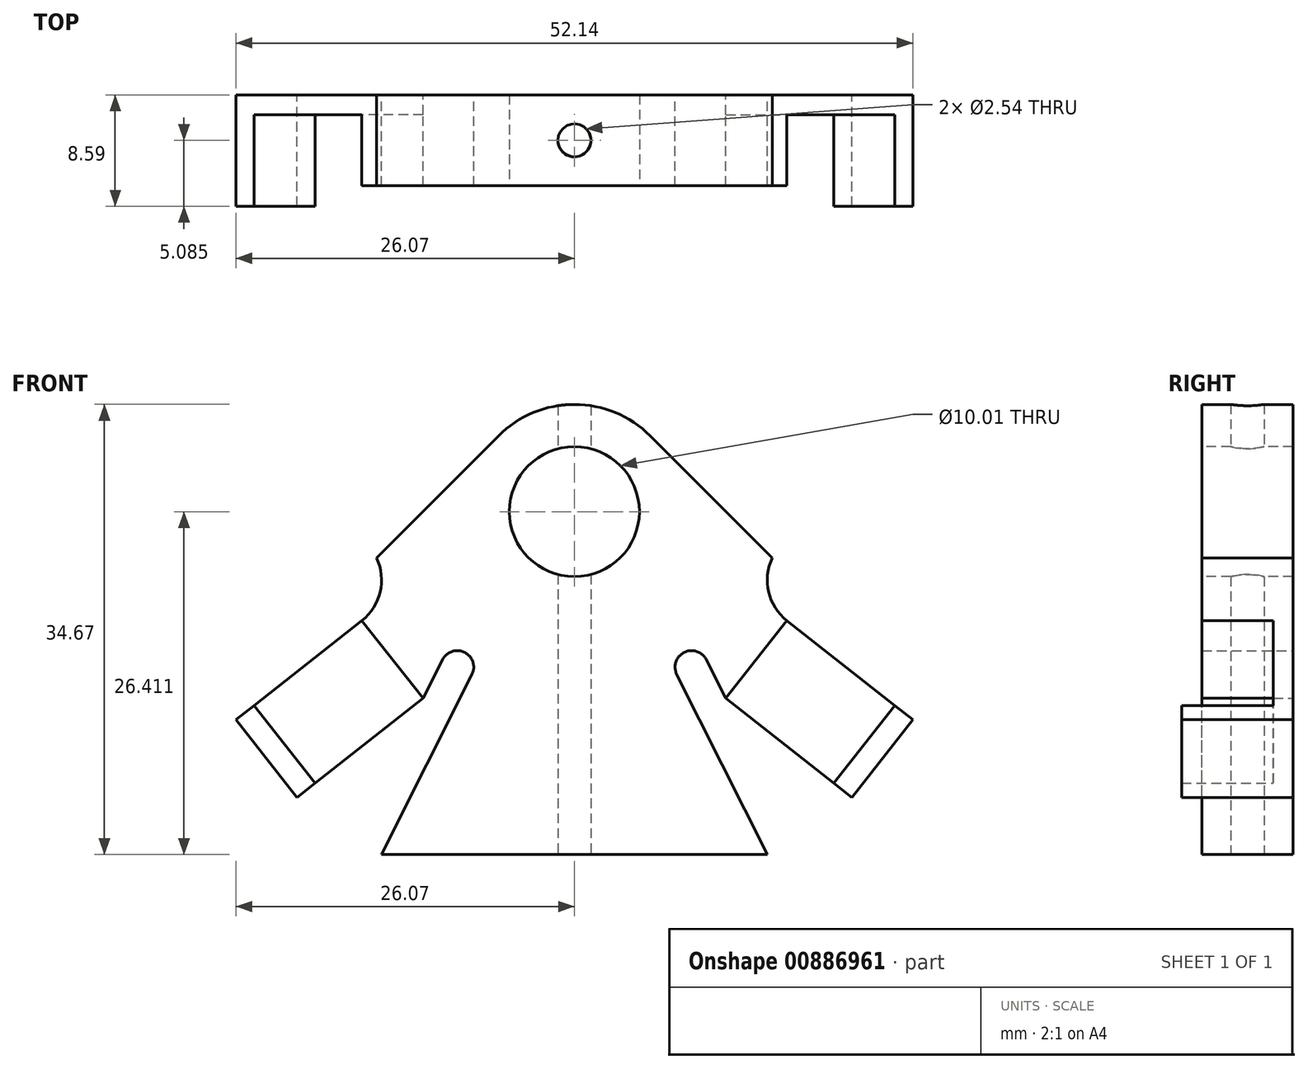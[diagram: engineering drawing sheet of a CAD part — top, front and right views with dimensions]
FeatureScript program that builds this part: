
annotation { "Feature Type Name" : "Feature", "Feature Type Description" : "" }
export const myFeature = defineFeature(function(context is Context, id is Id, definition is map)
    precondition{}
    {
        {
            var Q0;
            Q0=qCreatedBy(makeId("Front.planeOp"),FACE);
            var sketch = newSketch(context, id + "F0", { "sketchPlane" : qUnion([Q0])});
            skLineSegment(sketch, "E0", {"start": v(0, 0) * mm, "end": v(14.86, 0) * mm});
            skLineSegment(sketch, "E1", {"start": v(14.86, 0) * mm, "end": v(7.9, 13.87) * mm});
            skArc(sketch, "E2", {"start": v(7.9, 13.87) * mm, "mid": v(8.46, 15.57) * mm, "end": v(10.16, 15) * mm});
            skLineSegment(sketch, "E3", {"start": v(10.16, 15) * mm, "end": v(11.65, 12.03) * mm});
            skLineSegment(sketch, "E4", {"start": v(11.65, 12.03) * mm, "end": v(19.96, 5.5) * mm});
            skLineSegment(sketch, "E5", {"start": v(19.96, 5.5) * mm, "end": v(21.36, 4.4) * mm});
            skLineSegment(sketch, "E6", {"start": v(21.36, 4.4) * mm, "end": v(26.07, 10.39) * mm});
            skLineSegment(sketch, "E7", {"start": v(26.07, 10.39) * mm, "end": v(16.37, 18.02) * mm});
            skArc(sketch, "E8", {"start": v(16.37, 18.02) * mm, "mid": v(14.96, 20.24) * mm, "end": v(15.24, 22.85) * mm});
            skLineSegment(sketch, "E9", {"start": v(15.24, 22.85) * mm, "end": v(0, 38.09) * mm});
            skLineSegment(sketch, "E10", {"start": v(0, 38.09) * mm, "end": v(0, 0) * mm});
            skLineSegment(sketch, "E11.MirrorCS", {"start": v(-19.96, 5.5) * mm, "end": v(-21.36, 4.4) * mm});
            skLineSegment(sketch, "E12.MirrorCS", {"start": v(0, 0) * mm, "end": v(-14.86, 0) * mm});
            skLineSegment(sketch, "E13.MirrorCS", {"start": v(-14.86, 0) * mm, "end": v(-7.9, 13.87) * mm});
            skArc(sketch, "E14.MirrorCS", {"start": v(-7.9, 13.87) * mm, "mid": v(-8.46, 15.57) * mm, "end": v(-10.16, 15) * mm});
            skLineSegment(sketch, "E15.MirrorCS", {"start": v(-10.16, 15) * mm, "end": v(-11.65, 12.03) * mm});
            skLineSegment(sketch, "E16.MirrorCS", {"start": v(-11.65, 12.03) * mm, "end": v(-19.96, 5.5) * mm});
            skLineSegment(sketch, "E17.MirrorCS", {"start": v(-21.36, 4.4) * mm, "end": v(-26.07, 10.39) * mm});
            skLineSegment(sketch, "E18.MirrorCS", {"start": v(-26.07, 10.39) * mm, "end": v(-16.37, 18.02) * mm});
            skArc(sketch, "E19.MirrorCS", {"start": v(-16.37, 18.02) * mm, "mid": v(-14.96, 20.24) * mm, "end": v(-15.24, 22.85) * mm});
            skLineSegment(sketch, "E20.MirrorCS", {"start": v(-15.24, 22.85) * mm, "end": v(0, 38.09) * mm});
            skSolve(sketch);
        }
        {
            var Q0;
            Q0=makeQuery(id+"F0.imprint","IMPRINT",FACE,{"disambiguationData":[TD([[makeQuery(id+"F0.imprint","IMPRINT",EDGE,{"derivedFrom":sQuery(id+"F0.wireOp",EDGE,"E0")}),1.0]])]});
            var Q1;
            Q1=makeQuery(id+"F0.imprint","IMPRINT",FACE,{"disambiguationData":[TD([[makeQuery(id+"F0.imprint","IMPRINT",EDGE,{"derivedFrom":sQuery(id+"F0.wireOp",EDGE,"E10")}),-1.0]])]});
            extrude(context, id + "F1", {"entities" : qUnion([Q0, Q1]), "depth" : 1.52 * mm, "offsetDistance" : 25.4 * mm});
        }
        {
            var Q0;
            Q0=makeQuery(id+"F1.opExtrude","SWEPT_EDGE",EDGE,{"disambiguationData":[OSD([sQuery(id+"F0.wireOp",EDGE,"E9"),sQuery(id+"F0.wireOp",EDGE,"E10"),sQuery(id+"F0.wireOp",EDGE,"E20.MirrorCS")])]});
            fillet(context, id + "F2", {"entities" : qUnion([Q0]), "radius" : 8.25 * mm, "tangentPropagation" : true, "allowEdgeOverflow" : false});
        }
        {
            var Q0;
            Q0=makeQuery(id+"F1.opExtrude","CAP_FACE",FACE,{"disambiguationData":[OSD([sQuery(id+"F0.wireOp",EDGE,"E0"),sQuery(id+"F0.wireOp",EDGE,"E1"),sQuery(id+"F0.wireOp",EDGE,"E2"),sQuery(id+"F0.wireOp",EDGE,"E3"),sQuery(id+"F0.wireOp",EDGE,"E4"),sQuery(id+"F0.wireOp",EDGE,"E5"),sQuery(id+"F0.wireOp",EDGE,"E6"),sQuery(id+"F0.wireOp",EDGE,"E7"),sQuery(id+"F0.wireOp",EDGE,"E8"),sQuery(id+"F0.wireOp",EDGE,"E9"),sQuery(id+"F0.wireOp",EDGE,"E11.MirrorCS"),sQuery(id+"F0.wireOp",EDGE,"E12.MirrorCS"),sQuery(id+"F0.wireOp",EDGE,"E13.MirrorCS"),sQuery(id+"F0.wireOp",EDGE,"E14.MirrorCS"),sQuery(id+"F0.wireOp",EDGE,"E15.MirrorCS"),sQuery(id+"F0.wireOp",EDGE,"E16.MirrorCS"),sQuery(id+"F0.wireOp",EDGE,"E17.MirrorCS"),sQuery(id+"F0.wireOp",EDGE,"E18.MirrorCS"),sQuery(id+"F0.wireOp",EDGE,"E19.MirrorCS"),sQuery(id+"F0.wireOp",EDGE,"E20.MirrorCS")])],"isStart":false});
            var sketch = newSketch(context, id + "F3", { "sketchPlane" : qUnion([Q0])});
            skLineSegment(sketch, "E21", {"start": v(0, 34.67) * mm, "end": v(0, 26.41) * mm});
            skCircle(sketch, "E22", {"center": v(0, 26.41) * mm, "radius": 5 * mm});
            skSolve(sketch);
        }
        {
            var Q0;
            Q0=makeQuery(id+"F3.imprint","IMPRINT",FACE,{"disambiguationData":[TD([[makeQuery(id+"F3.imprint","IMPRINT",EDGE,{"derivedFrom":sQuery(id+"F3.wireOp",EDGE,"E22")}),1.0]])]});
            extrude(context, id + "F4", {"entities" : qUnion([Q0]), "operationType" : NewBodyOperationType.REMOVE, "oppositeDirection" : true, "depth" : 25.4 * mm, "offsetDistance" : 25.4 * mm});
        }
        {
            var Q0;
            Q0=makeQuery(id+"F1.opExtrude","CAP_FACE",FACE,{"disambiguationData":[OSD([sQuery(id+"F0.wireOp",EDGE,"E0"),sQuery(id+"F0.wireOp",EDGE,"E1"),sQuery(id+"F0.wireOp",EDGE,"E2"),sQuery(id+"F0.wireOp",EDGE,"E3"),sQuery(id+"F0.wireOp",EDGE,"E4"),sQuery(id+"F0.wireOp",EDGE,"E5"),sQuery(id+"F0.wireOp",EDGE,"E6"),sQuery(id+"F0.wireOp",EDGE,"E7"),sQuery(id+"F0.wireOp",EDGE,"E8"),sQuery(id+"F0.wireOp",EDGE,"E9"),sQuery(id+"F0.wireOp",EDGE,"E11.MirrorCS"),sQuery(id+"F0.wireOp",EDGE,"E12.MirrorCS"),sQuery(id+"F0.wireOp",EDGE,"E13.MirrorCS"),sQuery(id+"F0.wireOp",EDGE,"E14.MirrorCS"),sQuery(id+"F0.wireOp",EDGE,"E15.MirrorCS"),sQuery(id+"F0.wireOp",EDGE,"E16.MirrorCS"),sQuery(id+"F0.wireOp",EDGE,"E17.MirrorCS"),sQuery(id+"F0.wireOp",EDGE,"E18.MirrorCS"),sQuery(id+"F0.wireOp",EDGE,"E19.MirrorCS"),sQuery(id+"F0.wireOp",EDGE,"E20.MirrorCS")])],"isStart":false});
            var sketch = newSketch(context, id + "F5", { "sketchPlane" : qUnion([Q0])});
            skLineSegment(sketch, "E23.0.0", {"start": v(15.24, 22.85) * mm, "end": v(5.84, 32.25) * mm});
            skArc(sketch, "E23.0.1", {"start": v(5.84, 32.25) * mm, "mid": v(0, 34.67) * mm, "end": v(-5.84, 32.25) * mm});
            skLineSegment(sketch, "E23.0.2", {"start": v(-5.84, 32.25) * mm, "end": v(-15.24, 22.85) * mm});
            skArc(sketch, "E23.0.3", {"start": v(-15.24, 22.85) * mm, "mid": v(-14.96, 20.24) * mm, "end": v(-16.37, 18.02) * mm});
            skLineSegment(sketch, "E23.0.7", {"start": v(-11.65, 12.03) * mm, "end": v(-10.16, 15) * mm});
            skArc(sketch, "E23.0.8", {"start": v(-10.16, 15) * mm, "mid": v(-8.46, 15.57) * mm, "end": v(-7.9, 13.87) * mm});
            skLineSegment(sketch, "E23.0.9", {"start": v(-7.9, 13.87) * mm, "end": v(-14.86, 0) * mm});
            skLineSegment(sketch, "E23.0.10", {"start": v(-14.86, 0) * mm, "end": v(14.86, 0) * mm});
            skLineSegment(sketch, "E23.0.11", {"start": v(14.86, 0) * mm, "end": v(7.9, 13.87) * mm});
            skArc(sketch, "E23.0.12", {"start": v(7.9, 13.87) * mm, "mid": v(8.46, 15.57) * mm, "end": v(10.16, 15) * mm});
            skLineSegment(sketch, "E23.0.13", {"start": v(10.16, 15) * mm, "end": v(11.65, 12.03) * mm});
            skArc(sketch, "E23.0.17", {"start": v(16.37, 18.02) * mm, "mid": v(14.96, 20.24) * mm, "end": v(15.24, 22.85) * mm});
            skLineSegment(sketch, "E24", {"start": v(11.65, 12.03) * mm, "end": v(16.37, 18.02) * mm});
            skLineSegment(sketch, "E25", {"start": v(-11.65, 12.03) * mm, "end": v(-16.37, 18.02) * mm});
            skSolve(sketch);
        }
        {
            var Q0;
            Q0=makeQuery(id+"F5.imprint","IMPRINT",FACE,{"disambiguationData":[TD([[makeQuery(id+"F5.imprint","IMPRINT",EDGE,{"derivedFrom":sQuery(id+"F5.wireOp",EDGE,"E23.0.0")}),1.0]])]});
            extrude(context, id + "F6", {"entities" : qUnion([Q0]), "operationType" : NewBodyOperationType.ADD, "depth" : 5.5 * mm, "offsetDistance" : 25.4 * mm});
        }
        {
            var Q0;
            {var subQ0=sQuery(id+"F0.wireOp",EDGE,"E7");var subQ1=sQuery(id+"F0.wireOp",EDGE,"E6");var subQ2=sQuery(id+"F0.wireOp",EDGE,"E5");var subQ3=sQuery(id+"F0.wireOp",EDGE,"E4");var subQ4=sQuery(id+"F0.wireOp",EDGE,"E3");var subQ5=sQuery(id+"F0.wireOp",EDGE,"E8");Q0=makeQuery(id+"F6.boolean.opBoolean","SPLIT",FACE,{"disambiguationData":[TD([makeQuery(id+"F1.opExtrude","SWEPT_FACE",FACE,{"disambiguationData":[OSD([subQ4])]})])],"derivedFrom":makeQuery(id+"F1.opExtrude","CAP_FACE",FACE,{"disambiguationData":[OSD([sQuery(id+"F0.wireOp",EDGE,"E0"),sQuery(id+"F0.wireOp",EDGE,"E1"),sQuery(id+"F0.wireOp",EDGE,"E2"),subQ4,subQ3,subQ2,subQ1,subQ0,subQ5,sQuery(id+"F0.wireOp",EDGE,"E9"),sQuery(id+"F0.wireOp",EDGE,"E11.MirrorCS"),sQuery(id+"F0.wireOp",EDGE,"E12.MirrorCS"),sQuery(id+"F0.wireOp",EDGE,"E13.MirrorCS"),sQuery(id+"F0.wireOp",EDGE,"E14.MirrorCS"),sQuery(id+"F0.wireOp",EDGE,"E15.MirrorCS"),sQuery(id+"F0.wireOp",EDGE,"E16.MirrorCS"),sQuery(id+"F0.wireOp",EDGE,"E17.MirrorCS"),sQuery(id+"F0.wireOp",EDGE,"E18.MirrorCS"),sQuery(id+"F0.wireOp",EDGE,"E19.MirrorCS"),sQuery(id+"F0.wireOp",EDGE,"E20.MirrorCS")])],"isStart":false})});}
            var sketch = newSketch(context, id + "F7", { "sketchPlane" : qUnion([Q0])});
            skLineSegment(sketch, "E26.0", {"start": v(21.36, 4.4) * mm, "end": v(26.07, 10.39) * mm});
            skLineSegment(sketch, "E27", {"start": v(21.36, 4.4) * mm, "end": v(19.96, 5.5) * mm});
            skLineSegment(sketch, "E28", {"start": v(19.96, 5.5) * mm, "end": v(24.67, 11.49) * mm});
            skLineSegment(sketch, "E29", {"start": v(24.67, 11.49) * mm, "end": v(26.07, 10.39) * mm});
            skLineSegment(sketch, "E30.MirrorCS", {"start": v(-24.67, 11.49) * mm, "end": v(-26.07, 10.39) * mm});
            skLineSegment(sketch, "E31.MirrorCS", {"start": v(-21.36, 4.4) * mm, "end": v(-19.96, 5.5) * mm});
            skLineSegment(sketch, "E32.MirrorCS", {"start": v(-19.96, 5.5) * mm, "end": v(-24.67, 11.49) * mm});
            skLineSegment(sketch, "E33.MirrorCS", {"start": v(-21.36, 4.4) * mm, "end": v(-26.07, 10.39) * mm});
            skSolve(sketch);
        }
        {
            var Q0;
            Q0 = qSketchRegion(id + "F7", true);
            extrude(context, id + "F8", {"entities" : qUnion([Q0]), "operationType" : NewBodyOperationType.ADD, "depth" : 7.06 * mm, "offsetDistance" : 25.4 * mm});
        }
        {
            var Q0;
            Q0=makeQuery(id+"F6.boolean.opBoolean","MERGE",FACE,{"derivedFrom":[makeQuery(id+"F1.opExtrude","SWEPT_FACE",FACE,{"disambiguationData":[OSD([sQuery(id+"F0.wireOp",EDGE,"E0"),sQuery(id+"F0.wireOp",EDGE,"E12.MirrorCS")])]}),makeQuery(id+"F6.opExtrude","SWEPT_FACE",FACE,{"disambiguationData":[OSD([sQuery(id+"F5.wireOp",EDGE,"E23.0.10")])]})]});
            var sketch = newSketch(context, id + "F9", { "sketchPlane" : qUnion([Q0])});
            skCircle(sketch, "E34", {"center": v(0, 3.5) * mm, "radius": 1.27 * mm});
            skPoint(sketch, "E34.centerSnap0", {"position": v(14.86, 3.5) * mm});
            skSolve(sketch);
        }
        {
            var Q0;
            Q0 = qSketchRegion(id + "F9", true);
            extrude(context, id + "F10", {"entities" : qUnion([Q0]), "operationType" : NewBodyOperationType.REMOVE, "endBound" : BoundingType.THROUGH_ALL, "oppositeDirection" : true, "depth" : 25.4 * mm, "offsetDistance" : 25.4 * mm});
        }
    });
